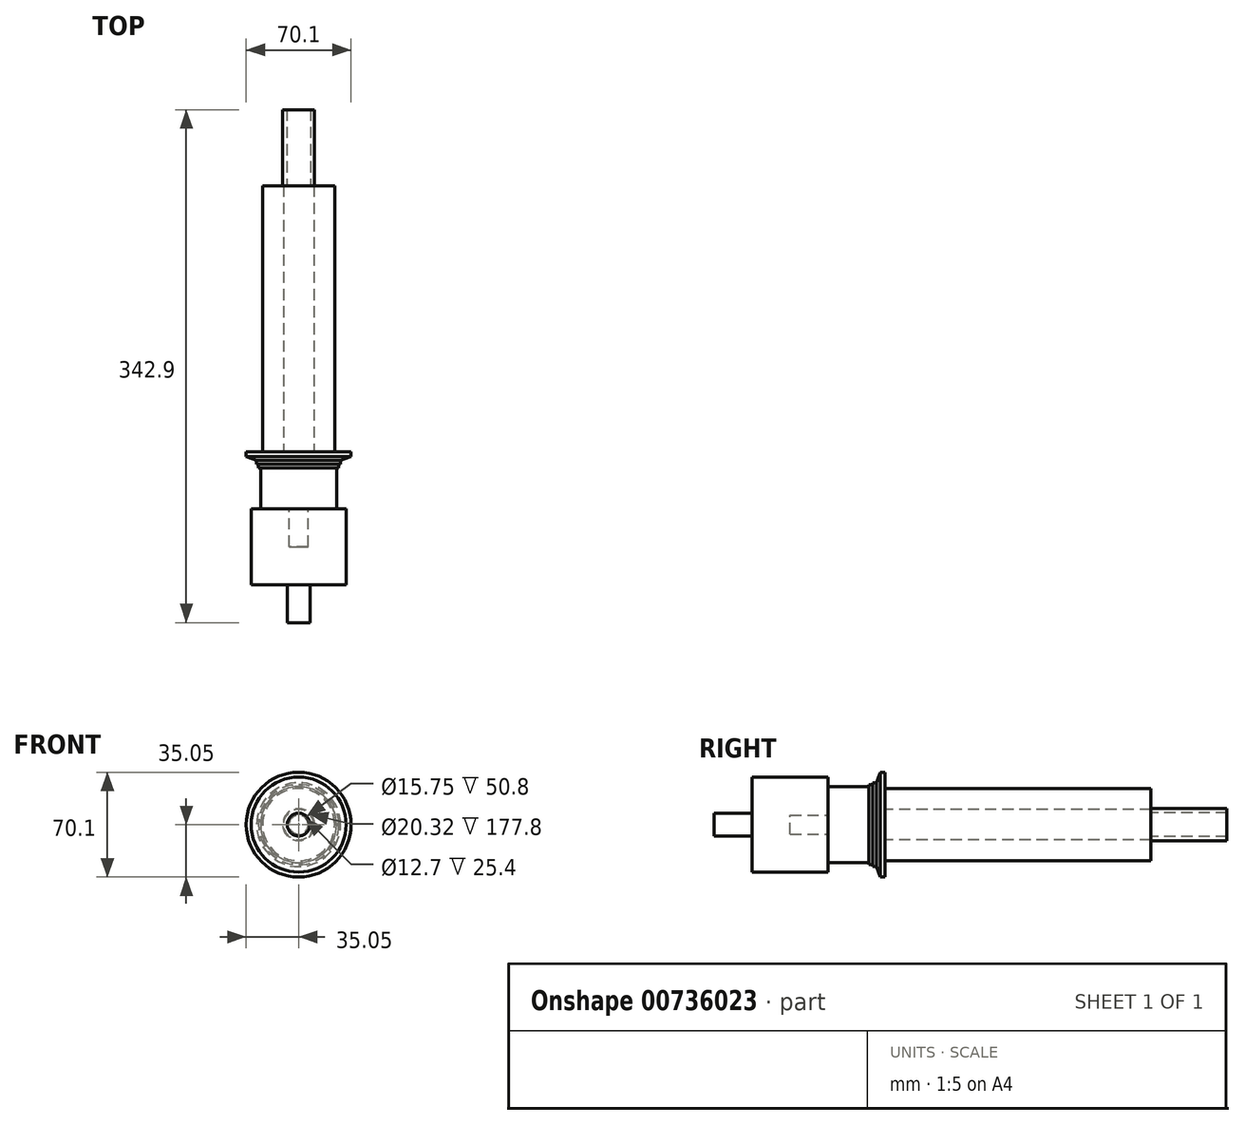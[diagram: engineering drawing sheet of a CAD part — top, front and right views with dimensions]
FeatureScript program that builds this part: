
annotation { "Feature Type Name" : "Feature", "Feature Type Description" : "" }
export const myFeature = defineFeature(function(context is Context, id is Id, definition is map)
    precondition{}
    {
        {
            var Q0;
            Q0=qCreatedBy(makeId("Front.planeOp"),FACE);
            var sketch = newSketch(context, id + "F0", { "sketchPlane" : qUnion([Q0])});
            skCircle(sketch, "E0", {"center": v(0, 0) * mm, "radius": 22.23 * mm, "construction": true});
            skSolve(sketch);
        }
        {
            var Q0;
            Q0=qCreatedBy(makeId("Front.planeOp"),FACE);
            var sketch = newSketch(context, id + "F1", { "sketchPlane" : qUnion([Q0])});
            skCircle(sketch, "E1", {"center": v(0, 0) * mm, "radius": 6.35 * mm});
            skSolve(sketch);
        }
        {
            var Q0;
            Q0=qSketchRegion(id+"F1",true);
            extrude(context, id + "F2", {"entities" : qUnion([Q0]), "oppositeDirection" : true, "depth" : 5.84 * mm, "offsetDistance" : 25.4 * mm});
        }
        {
            var Q0;
            Q0=makeQuery(id+"F2.opExtrude","CAP_FACE",FACE,{"disambiguationData":[OSD([sQuery(id+"F1.wireOp",EDGE,"qyfv2F2j-lcvM-QL7z-iw0u-FqIMPd33jrlv"),sQuery(id+"F1.wireOp",EDGE,"E1")])],"isStart":false});
            var sketch = newSketch(context, id + "F3", { "sketchPlane" : qUnion([Q0])});
            skCircle(sketch, "E2", {"center": v(0, 0) * mm, "radius": 6.35 * mm});
            skSolve(sketch);
        }
        {
            var Q0;
            Q0=qSketchRegion(id+"F3",true);
            extrude(context, id + "F4", {"entities" : qUnion([Q0]), "operationType" : NewBodyOperationType.ADD, "depth" : 2.54 * mm, "offsetDistance" : 25.4 * mm});
        }
        {
            var Q0;
            Q0=makeQuery(id+"F2.opExtrude","CAP_FACE",FACE,{"disambiguationData":[OSD([sQuery(id+"F1.wireOp",EDGE,"E1")])],"isStart":true});
            var sketch = newSketch(context, id + "F5", { "sketchPlane" : qUnion([Q0])});
            skCircle(sketch, "E3", {"center": v(0, 0) * mm, "radius": 31.75 * mm});
            skCircle(sketch, "E4", {"center": v(0, 0) * mm, "radius": 6.35 * mm});
            skSolve(sketch);
        }
        {
            var Q0;
            Q0=qSketchRegion(id+"F5",true);
            extrude(context, id + "F6", {"entities" : qUnion([Q0]), "operationType" : NewBodyOperationType.ADD, "depth" : 50.8 * mm, "offsetDistance" : 25.4 * mm});
        }
        {
            var Q0;
            Q0=makeQuery(id+"F6.opExtrude","CAP_FACE",FACE,{"disambiguationData":[OSD([sQuery(id+"F5.wireOp",EDGE,"E3"),sQuery(id+"F5.wireOp",EDGE,"E4")])],"isStart":false});
            var sketch = newSketch(context, id + "F7", { "sketchPlane" : qUnion([Q0])});
            skCircle(sketch, "E5", {"center": v(0, 0) * mm, "radius": 6.35 * mm});
            skCircle(sketch, "E6", {"center": v(0, 0) * mm, "radius": 7.62 * mm});
            skSolve(sketch);
        }
        {
            var Q0;
            Q0=qSketchRegion(id+"F7",true);
            extrude(context, id + "F8", {"entities" : qUnion([Q0]), "operationType" : NewBodyOperationType.ADD, "depth" : 25.4 * mm, "offsetDistance" : 25.4 * mm});
        }
        {
            var Q0;
            Q0=makeQuery(id+"F8.opExtrude","CAP_FACE",FACE,{"disambiguationData":[OSD([sQuery(id+"F7.wireOp",EDGE,"E5"),sQuery(id+"F7.wireOp",EDGE,"E6")])],"isStart":false});
            var sketch = newSketch(context, id + "F9", { "sketchPlane" : qUnion([Q0])});
            skCircle(sketch, "E7", {"center": v(0, 0) * mm, "radius": 6.35 * mm});
            skSolve(sketch);
        }
        {
            var Q0;
            Q0=qCreatedBy(makeId("Right.planeOp"),FACE);
            var sketch = newSketch(context, id + "F10", { "sketchPlane" : qUnion([Q0])});
            skLineSegment(sketch, "E8", {"start": v(-76.2, 0) * mm, "end": v(-25.4, 0) * mm});
            skSolve(sketch);
        }
        {
            var Q0;
            Q0=qSketchRegion(id+"F9",true);
            var Q1;
            Q1=qConstructionFilter(qBodyType(qCreatedBy(id+"F10",EDGE),BodyType.WIRE),ConstructionObject.NO);
            sweep(context, id + "F11", {"operationType" : NewBodyOperationType.ADD, "profiles" : qUnion([Q0]), "path" : qUnion([Q1])});
        }
        {
            var Q0;
            Q0=makeQuery(id+"F6.opExtrude","CAP_FACE",FACE,{"disambiguationData":[OSD([sQuery(id+"F5.wireOp",EDGE,"E3"),sQuery(id+"F5.wireOp",EDGE,"E4")])],"isStart":true});
            var sketch = newSketch(context, id + "F12", { "sketchPlane" : qUnion([Q0])});
            skCircle(sketch, "E9", {"center": v(0, 0) * mm, "radius": 25.4 * mm});
            skSolve(sketch);
        }
        {
            var Q0;
            Q0=qSketchRegion(id+"F12",true);
            extrude(context, id + "F13", {"entities" : qUnion([Q0]), "operationType" : NewBodyOperationType.ADD, "depth" : 38.1 * mm, "offsetDistance" : 25.4 * mm});
        }
        {
            var Q0;
            Q0=makeQuery(id+"F13.opExtrude","CAP_FACE",FACE,{"disambiguationData":[OSD([sQuery(id+"F12.wireOp",EDGE,"DsUQaM0h-b900-1fN3-LuSI-3gaKPxpTFhlT"),sQuery(id+"F12.wireOp",EDGE,"E9")])],"isStart":false});
            var sketch = newSketch(context, id + "F14", { "sketchPlane" : qUnion([Q0])});
            skCircle(sketch, "E10", {"center": v(0, 0) * mm, "radius": 35.05 * mm});
            skCircle(sketch, "E11", {"center": v(0, 0) * mm, "radius": 22.86 * mm});
            skSolve(sketch);
        }
        {
            var Q0;
            Q0=qSketchRegion(id+"F14",true);
            extrude(context, id + "F15", {"entities" : qUnion([Q0]), "operationType" : NewBodyOperationType.ADD, "oppositeDirection" : true, "depth" : 5.84 * mm, "offsetDistance" : 25.4 * mm});
        }
        {
            var Q0;
            Q0=makeQuery(id+"F15.opExtrude","CAP_EDGE",EDGE,{"disambiguationData":[OSD([sQuery(id+"F14.wireOp",EDGE,"E10")])],"isStart":false});
            chamfer(context, id + "F16", {"entities" : qUnion([Q0]), "chamferType" : ChamferType.OFFSET_ANGLE, "width" : 2.54 * mm, "oppositeDirection" : false, "angle" : 70 * degree, "tangentPropagation" : true});
        }
        {
            var Q0;
            Q0=makeQuery(id+"F15.opExtrude","CAP_FACE",FACE,{"disambiguationData":[OSD([sQuery(id+"F14.wireOp",EDGE,"E10"),sQuery(id+"F14.wireOp",EDGE,"E11")])],"isStart":false});
            var sketch = newSketch(context, id + "F17", { "sketchPlane" : qUnion([Q0])});
            skCircle(sketch, "E12", {"center": v(0, 0) * mm, "radius": 24.13 * mm});
            skCircle(sketch, "E13", {"center": v(0, 0) * mm, "radius": 28.07 * mm});
            skSolve(sketch);
        }
        {
            var Q0;
            Q0=qSketchRegion(id+"F17",true);
            extrude(context, id + "F18", {"entities" : qUnion([Q0]), "operationType" : NewBodyOperationType.ADD, "depth" : 2.54 * mm, "offsetDistance" : 25.4 * mm});
        }
        {
            var Q0;
            Q0=makeQuery(id+"F18.opExtrude","CAP_FACE",FACE,{"disambiguationData":[OSD([sQuery(id+"F17.wireOp",EDGE,"E12"),sQuery(id+"F17.wireOp",EDGE,"E13")])],"isStart":false});
            var sketch = newSketch(context, id + "F19", { "sketchPlane" : qUnion([Q0])});
            skCircle(sketch, "E14", {"center": v(0, 0) * mm, "radius": 24.13 * mm});
            skCircle(sketch, "E15", {"center": v(0, 0) * mm, "radius": 26.8 * mm});
            skSolve(sketch);
        }
        {
            var Q0;
            Q0=qSketchRegion(id+"F19",true);
            extrude(context, id + "F20", {"entities" : qUnion([Q0]), "operationType" : NewBodyOperationType.ADD, "depth" : 2.54 * mm, "offsetDistance" : 25.4 * mm});
        }
        {
            var Q0;
            Q0=makeQuery(id+"F15.boolean.opBoolean","MERGE",FACE,{"derivedFrom":[makeQuery(id+"F13.opExtrude","CAP_FACE",FACE,{"disambiguationData":[OSD([sQuery(id+"F12.wireOp",EDGE,"DsUQaM0h-b900-1fN3-LuSI-3gaKPxpTFhlT"),sQuery(id+"F12.wireOp",EDGE,"E9")])],"isStart":false}),makeQuery(id+"F15.opExtrude","CAP_FACE",FACE,{"disambiguationData":[OSD([sQuery(id+"F14.wireOp",EDGE,"E10"),sQuery(id+"F14.wireOp",EDGE,"E11")])],"isStart":true})]});
            var sketch = newSketch(context, id + "F21", { "sketchPlane" : qUnion([Q0])});
            skCircle(sketch, "E16", {"center": v(0, 0) * mm, "radius": 10.16 * mm});
            skCircle(sketch, "E17", {"center": v(0, 0) * mm, "radius": 24.13 * mm});
            skSolve(sketch);
        }
        {
            var Q0;
            Q0=qSketchRegion(id+"F21",true);
            extrude(context, id + "F22", {"entities" : qUnion([Q0]), "operationType" : NewBodyOperationType.ADD, "depth" : 177.8 * mm, "offsetDistance" : 25.4 * mm});
        }
        {
            var Q0;
            Q0=makeQuery(id+"F22.opExtrude","CAP_FACE",FACE,{"disambiguationData":[OSD([sQuery(id+"F21.wireOp",EDGE,"E16"),sQuery(id+"F21.wireOp",EDGE,"E17")])],"isStart":false});
            var sketch = newSketch(context, id + "F23", { "sketchPlane" : qUnion([Q0])});
            skCircle(sketch, "E18", {"center": v(0, 0) * mm, "radius": 10.67 * mm});
            skCircle(sketch, "E19", {"center": v(0, 0) * mm, "radius": 7.87 * mm});
            skSolve(sketch);
        }
        {
            var Q0;
            Q0=qSketchRegion(id+"F23",true);
            extrude(context, id + "F24", {"entities" : qUnion([Q0]), "operationType" : NewBodyOperationType.ADD, "depth" : 50.8 * mm, "offsetDistance" : 25.4 * mm});
        }
    });
